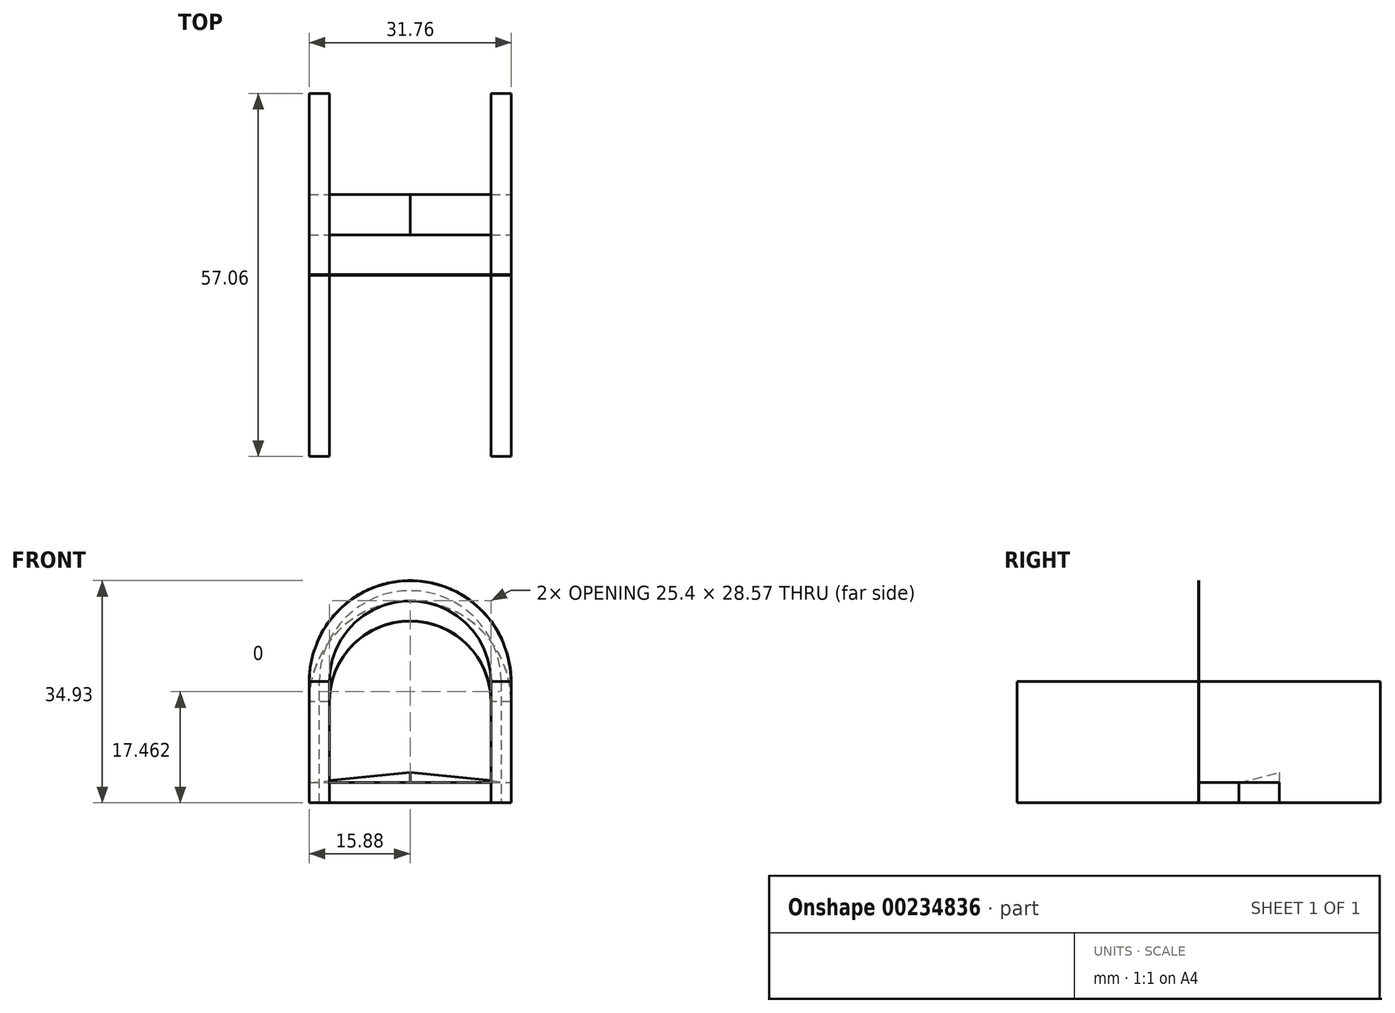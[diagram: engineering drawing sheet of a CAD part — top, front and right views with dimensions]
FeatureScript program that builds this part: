
annotation { "Feature Type Name" : "Feature", "Feature Type Description" : "" }
export const myFeature = defineFeature(function(context is Context, id is Id, definition is map)
    precondition{}
    {
        {
            var Q0;
            Q0=qCreatedBy(makeId("Top.planeOp"),FACE);
            var sketch = newSketch(context, id + "F0", { "sketchPlane" : qUnion([Q0])});
            skLineSegment(sketch, "E0.bottom", {"start": v(15.88, 28.58) * mm, "end": v(-15.88, 28.58) * mm});
            skLineSegment(sketch, "E0.top", {"start": v(15.88, -28.58) * mm, "end": v(-15.88, -28.58) * mm});
            skLineSegment(sketch, "E0.left", {"start": v(15.88, 28.58) * mm, "end": v(15.88, -28.58) * mm});
            skLineSegment(sketch, "E0.right", {"start": v(-15.88, 28.58) * mm, "end": v(-15.88, -28.58) * mm});
            skPoint(sketch, "E0.middle", {"position": v(0, 0) * mm});
            skSolve(sketch);
        }
        {
            var Q0;
            Q0=qCreatedBy(makeId("Front.planeOp"),FACE);
            cPlane(context, id + "F1", {"entities" : qUnion([Q0]), "cplaneType" : CPlaneType.OFFSET, "offset" : 2.25 / 50.8 * mm, "oppositeDirection" : true, "width" : 152.4 * mm, "height" : 152.4 * mm});
        }
        {
            var Q0;
            Q0=qCreatedBy(id+"F1.planeOp",FACE);
            var sketch = newSketch(context, id + "F2", { "sketchPlane" : qUnion([Q0])});
            skLineSegment(sketch, "E1.0", {"start": v(15.88, 0) * mm, "end": v(-15.88, 0) * mm});
            skLineSegment(sketch, "E2", {"start": v(-15.88, 0) * mm, "end": v(-15.88, 19.05) * mm});
            skLineSegment(sketch, "E3", {"start": v(-15.88, 19.05) * mm, "end": v(15.88, 19.05) * mm, "construction": true});
            skLineSegment(sketch, "E4", {"start": v(15.88, 19.05) * mm, "end": v(15.88, 0) * mm});
            skArc(sketch, "E5", {"start": v(15.88, 19.05) * mm, "mid": v(0, 34.93) * mm, "end": v(-15.88, 19.05) * mm});
            skLineSegment(sketch, "E6.0", {"start": v(-22.22, 0) * mm, "end": v(-22.22, 19.05) * mm, "construction": true});
            skLineSegment(sketch, "E7.0", {"start": v(12.7, 19.05) * mm, "end": v(12.7, 0) * mm});
            skArc(sketch, "E7.1", {"start": v(12.7, 19.05) * mm, "mid": v(0, 31.75) * mm, "end": v(-12.7, 19.05) * mm});
            skLineSegment(sketch, "E7.2", {"start": v(-12.7, 0) * mm, "end": v(-12.7, 19.05) * mm});
            skLineSegment(sketch, "E8", {"start": v(12.7, 3.18) * mm, "end": v(-12.7, 3.18) * mm});
            skSolve(sketch);
        }
        {
            var Q0;
            Q0 = qSketchRegion(id + "F2", true);
            extrude(context, id + "F3", {"entities" : qUnion([Q0]), "oppositeDirection" : true, "depth" : 1 / 406.4 * mm});
        }
        {
            var Q0;
            Q0=makeQuery(id+"F3.opExtrude","CAP_FACE",FACE,{"disambiguationData":[OSD([sQuery(id+"F2.wireOp",EDGE,"E1.0"),sQuery(id+"F2.wireOp",EDGE,"E2"),sQuery(id+"F2.wireOp",EDGE,"E4"),sQuery(id+"F2.wireOp",EDGE,"E5"),sQuery(id+"F2.wireOp",EDGE,"E7.0"),sQuery(id+"F2.wireOp",EDGE,"E7.1"),sQuery(id+"F2.wireOp",EDGE,"E7.2"),sQuery(id+"F2.wireOp",EDGE,"E8")])],"isStart":false});
            var sketch = newSketch(context, id + "F4", { "sketchPlane" : qUnion([Q0])});
            skLineSegment(sketch, "E9.0", {"start": v(15.88, 0) * mm, "end": v(15.88, 19.05) * mm});
            skArc(sketch, "E9.1", {"start": v(-15.88, 19.05) * mm, "mid": v(0, 34.93) * mm, "end": v(15.88, 19.05) * mm});
            skLineSegment(sketch, "E9.2", {"start": v(-15.88, 0) * mm, "end": v(15.88, 0) * mm});
            skLineSegment(sketch, "E9.3", {"start": v(-15.88, 19.05) * mm, "end": v(-15.88, 0) * mm});
            skLineSegment(sketch, "E10.0", {"start": v(-14.29, 19.05) * mm, "end": v(-14.29, 0) * mm});
            skArc(sketch, "E10.1", {"start": v(-14.29, 19.05) * mm, "mid": v(0, 33.34) * mm, "end": v(14.29, 19.05) * mm});
            skLineSegment(sketch, "E10.2", {"start": v(14.29, 0) * mm, "end": v(14.29, 19.05) * mm});
            skSolve(sketch);
        }
        {
            var Q0;
            {var subQ1=sQuery(id+"F4.wireOp",EDGE,"E9.0");Q0=makeQuery(id+"F4.imprint","IMPRINT",FACE,{"disambiguationData":[TD([[makeQuery(id+"F4.imprint","IMPRINT",EDGE,{"derivedFrom":subQ1}),1.0]])]});}
            extrude(context, id + "F5", {"entities" : qUnion([Q0]), "operationType" : NewBodyOperationType.ADD, "depth" : 1 / 406.4 * mm});
        }
        {
            var Q0;
            Q0=makeQuery(id+"F5.opExtrude","CAP_FACE",FACE,{"disambiguationData":[OSD([sQuery(id+"F4.wireOp",EDGE,"E9.0"),sQuery(id+"F4.wireOp",EDGE,"E9.1"),sQuery(id+"F4.wireOp",EDGE,"E9.2"),sQuery(id+"F4.wireOp",EDGE,"E9.3"),sQuery(id+"F4.wireOp",EDGE,"E10.0"),sQuery(id+"F4.wireOp",EDGE,"E10.1"),sQuery(id+"F4.wireOp",EDGE,"E10.2")])],"isStart":false});
            var sketch = newSketch(context, id + "F6", { "sketchPlane" : qUnion([Q0])});
            skArc(sketch, "E11.0", {"start": v(-15.88, 19.05) * mm, "mid": v(0, 34.93) * mm, "end": v(15.88, 19.05) * mm});
            skLineSegment(sketch, "E12.0", {"start": v(15.88, 0) * mm, "end": v(15.88, 19.05) * mm});
            skLineSegment(sketch, "E13.0", {"start": v(-15.88, 0) * mm, "end": v(15.88, 0) * mm});
            skLineSegment(sketch, "E14.0", {"start": v(-15.88, 19.05) * mm, "end": v(-15.88, 0) * mm});
            skLineSegment(sketch, "E15.0", {"start": v(12.7, 3.18) * mm, "end": v(12.7, 19.05) * mm});
            skLineSegment(sketch, "E15.1", {"start": v(-12.7, 3.18) * mm, "end": v(12.7, 3.18) * mm});
            skLineSegment(sketch, "E15.2", {"start": v(-12.7, 19.05) * mm, "end": v(-12.7, 3.18) * mm});
            skArc(sketch, "E15.3", {"start": v(-12.7, 19.05) * mm, "mid": v(0, 31.75) * mm, "end": v(12.7, 19.05) * mm});
            skSolve(sketch);
        }
        {
            var Q0;
            Q0 = qSketchRegion(id + "F6", true);
            extrude(context, id + "F7", {"entities" : qUnion([Q0]), "operationType" : NewBodyOperationType.ADD, "depth" : 1 / 406.4 * mm});
        }
        {
            var Q0;
            Q0=qCreatedBy(makeId("Front.planeOp"),FACE);
            var sketch = newSketch(context, id + "F8", { "sketchPlane" : qUnion([Q0])});
            skLineSegment(sketch, "E16.0", {"start": v(15.88, 19.05) * mm, "end": v(15.88, 0) * mm, "construction": true});
            skLineSegment(sketch, "E17.0", {"start": v(15.88, 0) * mm, "end": v(-15.88, 0) * mm});
            skLineSegment(sketch, "E18.0", {"start": v(12.7, 3.18) * mm, "end": v(-12.7, 3.18) * mm});
            skLineSegment(sketch, "E19.0", {"start": v(-15.88, 0) * mm, "end": v(-15.88, 19.05) * mm, "construction": true});
            skArc(sketch, "E20.0", {"start": v(15.88, 19.05) * mm, "mid": v(0, 34.93) * mm, "end": v(-15.88, 19.05) * mm, "construction": true});
            skLineSegment(sketch, "E21", {"start": v(15.88, 0) * mm, "end": v(15.88, 15.88) * mm});
            skLineSegment(sketch, "E22", {"start": v(15.88, 15.88) * mm, "end": v(-15.88, 15.87) * mm});
            skLineSegment(sketch, "E23", {"start": v(-15.87, 15.87) * mm, "end": v(-15.88, 0) * mm});
            skArc(sketch, "E24", {"start": v(15.88, 15.88) * mm, "mid": v(0, 31.75) * mm, "end": v(-15.88, 15.88) * mm});
            skArc(sketch, "E25.0", {"start": v(12.7, 15.88) * mm, "mid": v(0, 28.58) * mm, "end": v(-12.7, 15.88) * mm});
            skLineSegment(sketch, "E26.0", {"start": v(-12.7, 3.18) * mm, "end": v(-12.7, 15.88) * mm});
            skLineSegment(sketch, "E27.0", {"start": v(12.7, 15.88) * mm, "end": v(12.7, 3.18) * mm});
            skPoint(sketch, "E28.orphan", {"position": v(-12.7, 19.05) * mm});
            skPoint(sketch, "E29.orphan", {"position": v(12.7, 19.05) * mm});
            skSolve(sketch);
        }
        {
            var Q0;
            {var subQ5=sQuery(id+"F2.wireOp",EDGE,"E2");Q0=makeQuery(id+"F2.imprint","IMPRINT",FACE,{"disambiguationData":[TD([[makeQuery(id+"F2.imprint","IMPRINT",EDGE,{"derivedFrom":subQ5}),-1.0]])]});}
            var sketch = newSketch(context, id + "F9", { "sketchPlane" : qUnion([Q0])});
            skArc(sketch, "E30.0", {"start": v(15.88, 19.05) * mm, "mid": v(0, 34.93) * mm, "end": v(-15.88, 19.05) * mm});
            skArc(sketch, "E31.0", {"start": v(12.7, 19.05) * mm, "mid": v(0, 31.75) * mm, "end": v(-12.7, 19.05) * mm});
            skLineSegment(sketch, "E32", {"start": v(-12.7, 19.05) * mm, "end": v(-15.88, 19.05) * mm});
            skLineSegment(sketch, "E33", {"start": v(12.7, 19.05) * mm, "end": v(15.88, 19.05) * mm});
            skSolve(sketch);
        }
        {
            var Q0;
            {var subQ0=sQuery(id+"F8.wireOp",EDGE,"E24");Q0=makeQuery(id+"F8.imprint","IMPRINT",FACE,{"disambiguationData":[TD([[makeQuery(id+"F8.imprint","IMPRINT",EDGE,{"derivedFrom":subQ0}),1.0]])]});}
            var Q1;
            Q1=makeQuery(id+"F9.imprint","IMPRINT",FACE,{"disambiguationData":[TD([[makeQuery(id+"F9.imprint","IMPRINT",EDGE,{"derivedFrom":sQuery(id+"F9.wireOp",EDGE,"E30.0")}),1.0]])]});
            var Q2;
            {var subQ0=sQuery(id+"F8.wireOp",EDGE,"E24");Q2=makeQuery(id+"F8.imprint","IMPRINT",FACE,{"disambiguationData":[TD([[makeQuery(id+"F8.imprint","IMPRINT",EDGE,{"derivedFrom":subQ0}),1.0]])]});}
            var Q3;
            Q3=makeQuery(id+"F9.imprint","IMPRINT",FACE,{"disambiguationData":[TD([[makeQuery(id+"F9.imprint","IMPRINT",EDGE,{"derivedFrom":sQuery(id+"F9.wireOp",EDGE,"E30.0")}),1.0]])]});
            loft(context, id + "F10", {"sheetProfilesArray" : [{ "sheetProfileEntities" : qUnion([Q0]) }, { "sheetProfileEntities" : qUnion([Q1]) }], "wireProfilesArray" : [{ "wireProfileEntities" : qUnion([Q2]) }, { "wireProfileEntities" : qUnion([Q3]) }]});
        }
        {
            var Q0;
            Q0=makeQuery(id+"F9.imprint","IMPRINT",FACE,{"disambiguationData":[TD([[makeQuery(id+"F9.imprint","IMPRINT",EDGE,{"derivedFrom":sQuery(id+"F9.wireOp",EDGE,"E32")}),1.0]])]});
            var Q1;
            Q1=makeQuery(id+"F9.imprint","IMPRINT",FACE,{"disambiguationData":[TD([[makeQuery(id+"F9.imprint","IMPRINT",EDGE,{"derivedFrom":sQuery(id+"F9.wireOp",EDGE,"E33")}),-1.0]])]});
            extrude(context, id + "F11", {"entities" : qUnion([Q0, Q1]), "depth" : 28.57 * mm});
        }
        {
            var Q0;
            {var subQ0=sQuery(id+"F8.wireOp",EDGE,"E24");Q0=makeQuery(id+"F10.opLoft","SWEPT_BODY",BODY,{"disambiguationData":[OSD([makeQuery(id+"F8.imprint","IMPRINT",FACE,{"disambiguationData":[TD([[makeQuery(id+"F8.imprint","IMPRINT",EDGE,{"derivedFrom":subQ0}),1.0]])]}),makeQuery(id+"F9.imprint","IMPRINT",FACE,{"disambiguationData":[TD([[makeQuery(id+"F9.imprint","IMPRINT",EDGE,{"derivedFrom":sQuery(id+"F9.wireOp",EDGE,"E30.0")}),1.0]])]})])]});}
            var Q1;
            Q1=makeQuery(id+"F11.opExtrude","SWEPT_BODY",BODY,{"disambiguationData":[OSD([sQuery(id+"F2.wireOp",EDGE,"E1.0"),sQuery(id+"F2.wireOp",EDGE,"E2"),sQuery(id+"F2.wireOp",EDGE,"E7.2"),sQuery(id+"F9.wireOp",EDGE,"E32")])]});
            var Q2;
            Q2=makeQuery(id+"F11.opExtrude","SWEPT_BODY",BODY,{"disambiguationData":[OSD([sQuery(id+"F2.wireOp",EDGE,"E1.0"),sQuery(id+"F2.wireOp",EDGE,"E4"),sQuery(id+"F2.wireOp",EDGE,"E7.0"),sQuery(id+"F9.wireOp",EDGE,"E33")])]});
            var Q3;
            Q3=qCreatedBy(makeId("Front.planeOp"),FACE);
            mirror(context, id + "F12", {"entities" : qUnion([Q0, Q1, Q2]), "mirrorPlane" : qUnion([Q3])});
        }
        {
            var Q0;
            Q0=makeQuery(id+"F12.opPattern","COPY",FACE,{"derivedFrom":makeQuery(id+"F11.opExtrude","CAP_FACE",FACE,{"disambiguationData":[OSD([sQuery(id+"F2.wireOp",EDGE,"E1.0"),sQuery(id+"F2.wireOp",EDGE,"E2"),sQuery(id+"F2.wireOp",EDGE,"E7.2"),sQuery(id+"F9.wireOp",EDGE,"E32")])],"isStart":true}),"instanceName":"1"});
            var sketch = newSketch(context, id + "F13", { "sketchPlane" : qUnion([Q0])});
            skLineSegment(sketch, "E34.0", {"start": v(15.88, 0) * mm, "end": v(-15.88, 0) * mm});
            skLineSegment(sketch, "E35.0", {"start": v(-15.88, 0) * mm, "end": v(-15.88, 19.05) * mm});
            skLineSegment(sketch, "E36.0", {"start": v(-12.7, 0) * mm, "end": v(-12.7, 19.05) * mm});
            skLineSegment(sketch, "E37.0", {"start": v(12.7, 19.05) * mm, "end": v(12.7, 0) * mm});
            skLineSegment(sketch, "E38.0", {"start": v(15.88, 19.05) * mm, "end": v(15.88, 0) * mm});
            skLineSegment(sketch, "E39", {"start": v(-15.88, 3.17) * mm, "end": v(15.88, 3.17) * mm});
            skSolve(sketch);
        }
        {
            var Q0;
            Q0 = qSketchRegion(id + "F13", true);
            extrude(context, id + "F14", {"entities" : qUnion([Q0]), "oppositeDirection" : true, "depth" : 6.35 * mm});
        }
        {
            var Q0;
            Q0=makeQuery(id+"F14.opExtrude","CAP_FACE",FACE,{"disambiguationData":[OSD([sQuery(id+"F13.wireOp",EDGE,"E34.0"),sQuery(id+"F13.wireOp",EDGE,"E35.0"),sQuery(id+"F13.wireOp",EDGE,"E38.0"),sQuery(id+"F13.wireOp",EDGE,"E39")])],"isStart":false});
            cPlane(context, id + "F15", {"entities" : qUnion([Q0]), "cplaneType" : CPlaneType.OFFSET, "offset" : 6.35 * mm, "width" : 152.4 * mm, "height" : 152.4 * mm});
        }
        {
            var Q0;
            Q0=qCreatedBy(id+"F15.planeOp",FACE);
            var sketch = newSketch(context, id + "F16", { "sketchPlane" : qUnion([Q0])});
            skLineSegment(sketch, "E40.0", {"start": v(15.88, 3.17) * mm, "end": v(-15.88, 3.17) * mm, "construction": true});
            skLineSegment(sketch, "E41.0", {"start": v(-15.88, 0) * mm, "end": v(15.88, 0) * mm});
            skLineSegment(sketch, "E42.0", {"start": v(15.88, 0) * mm, "end": v(15.88, 3.17) * mm});
            skLineSegment(sketch, "E43.0", {"start": v(-15.88, 3.17) * mm, "end": v(-15.88, 0) * mm});
            skLineSegment(sketch, "E44", {"start": v(0, 3.17) * mm, "end": v(0, 4.76) * mm, "construction": true});
            skPoint(sketch, "E44.endSnap0", {"position": v(0, 3.17) * mm});
            skLineSegment(sketch, "E45", {"start": v(0, 4.76) * mm, "end": v(-15.88, 3.17) * mm});
            skLineSegment(sketch, "E46", {"start": v(15.88, 3.18) * mm, "end": v(0, 4.76) * mm});
            skSolve(sketch);
        }
        {
            var Q0;
            Q0=makeQuery(id+"F14.opExtrude","CAP_FACE",FACE,{"disambiguationData":[OSD([sQuery(id+"F13.wireOp",EDGE,"E34.0"),sQuery(id+"F13.wireOp",EDGE,"E35.0"),sQuery(id+"F13.wireOp",EDGE,"E38.0"),sQuery(id+"F13.wireOp",EDGE,"E39")])],"isStart":false});
            var Q1;
            Q1=makeQuery(id+"F16.imprint","IMPRINT",FACE,{"disambiguationData":[TD([[makeQuery(id+"F16.imprint","IMPRINT",EDGE,{"derivedFrom":sQuery(id+"F16.wireOp",EDGE,"E41.0")}),1.0]])]});
            var Q2;
            Q2=makeQuery(id+"F14.opExtrude","CAP_VERTEX",VERTEX,{"disambiguationData":[OSD([sQuery(id+"F13.wireOp",EDGE,"E35.0"),sQuery(id+"F13.wireOp",EDGE,"E39")])],"isStart":false});
            var Q3;
            Q3=sQuery(id+"F16.wireOp",VERTEX,"E40.0.start");
            loft(context, id + "F17", {"sheetProfilesArray" : [{ "sheetProfileEntities" : qUnion([Q0]) }, { "sheetProfileEntities" : qUnion([Q1]) }], "matchConnections" : true, "connections" : [{ "connectionEntities" : qUnion([Q2, Q3]), "connectionEdgeQueries" : qUnion([]), "connectionEdgeParameters" : [] }]});
        }
        {
            var Q0;
            Q0=qCreatedBy(id+"F15.planeOp",FACE);
            cPlane(context, id + "F18", {"entities" : qUnion([Q0]), "cplaneType" : CPlaneType.OFFSET, "offset" : 19.05 * mm, "width" : 152.4 * mm, "height" : 152.4 * mm});
        }
    });
